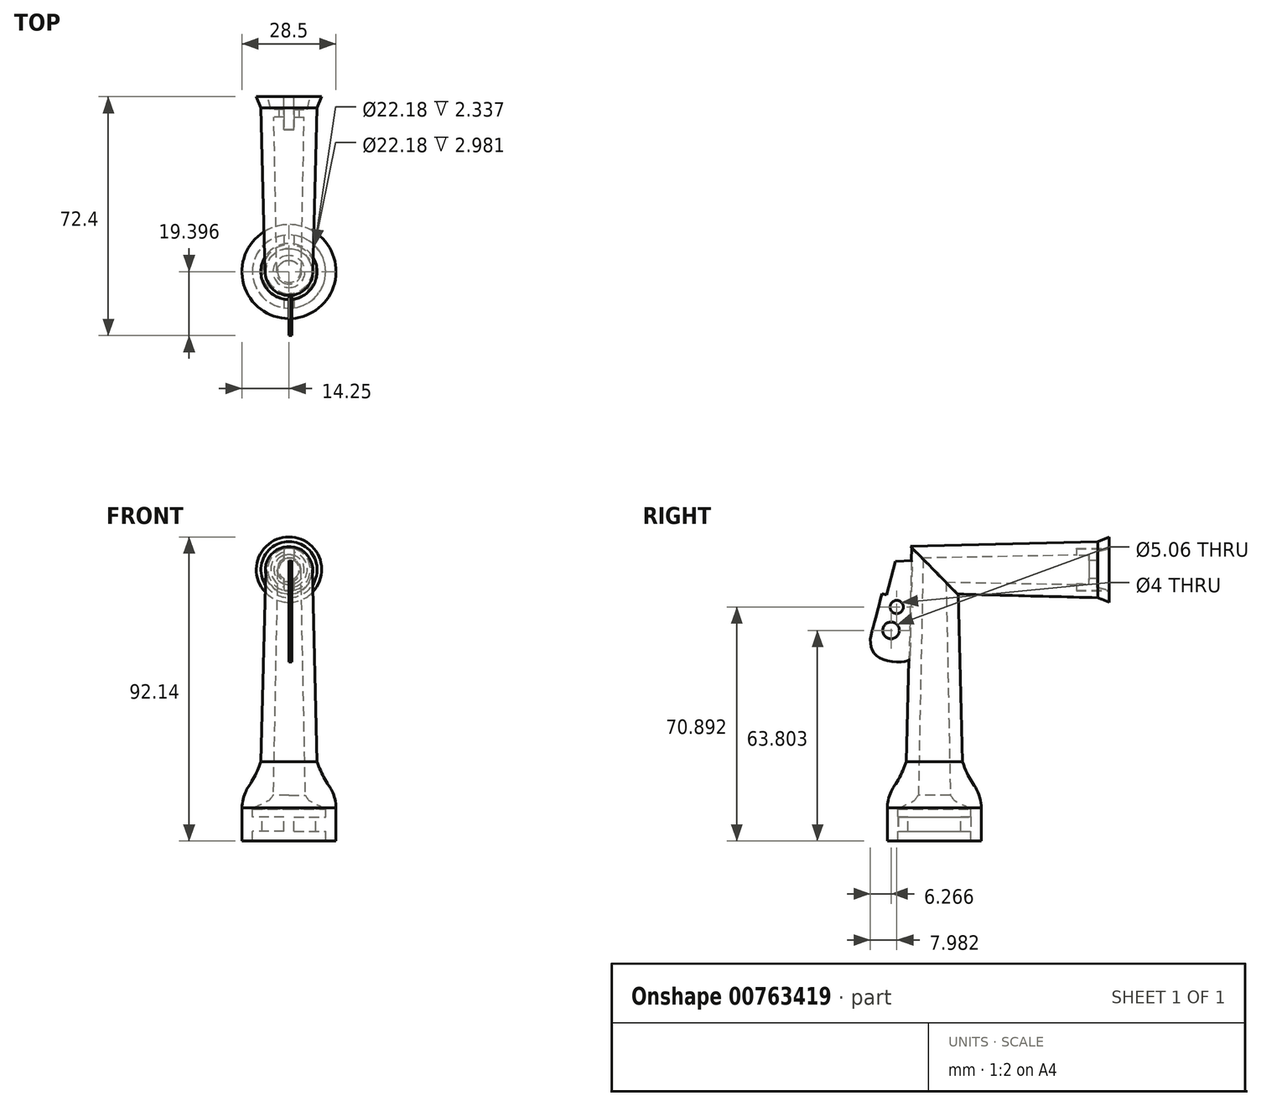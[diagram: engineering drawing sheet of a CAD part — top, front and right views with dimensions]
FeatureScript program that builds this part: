
annotation { "Feature Type Name" : "Feature", "Feature Type Description" : "" }
export const myFeature = defineFeature(function(context is Context, id is Id, definition is map)
    precondition{}
    {
        {
            var Q0;
            Q0=qCreatedBy(makeId("Right.planeOp"),FACE);
            var sketch = newSketch(context, id + "F0", { "sketchPlane" : qUnion([Q0])});
            skLineSegment(sketch, "E0", {"start": v(-40.8, 52.82) * mm, "end": v(-40.8, -26.68) * mm, "construction": true});
            skLineSegment(sketch, "E1", {"start": v(-26.55, -15.77) * mm, "end": v(-26.55, -25.77) * mm});
            skFitSpline(sketch, "E2", {"points": [v(-32.3, -1.7) * mm, v(-30.9, -5.15) * mm, v(-29, -8.6) * mm, v(-27.92, -10.27) * mm, v(-26.85, -13.25) * mm, v(-26.55, -15.77) * mm], "startDerivative": vector(5.6, -15.17) * mm, "endDerivative": vector(0.76, -13.15) * mm});
            skLineSegment(sketch, "E3", {"start": v(-26.55, -25.77) * mm, "end": v(-29.71, -25.77) * mm});
            skLineSegment(sketch, "E4", {"start": v(-29.71, -25.77) * mm, "end": v(-29.71, -22.79) * mm});
            skLineSegment(sketch, "E5", {"start": v(-29.71, -22.79) * mm, "end": v(-32.69, -22.79) * mm});
            skLineSegment(sketch, "E6", {"start": v(-32.69, -22.79) * mm, "end": v(-32.69, -18.47) * mm});
            skLineSegment(sketch, "E7", {"start": v(-32.69, -18.47) * mm, "end": v(-29.71, -18.47) * mm});
            skLineSegment(sketch, "E8", {"start": v(-29.71, -18.47) * mm, "end": v(-29.71, -16.13) * mm});
            skFitSpline(sketch, "E9", {"points": [v(-29.71, -16.13) * mm, v(-31.55, -15.07) * mm, v(-34.67, -13.51) * mm, v(-35.32, -12.81) * mm, v(-35.96, -11.89) * mm], "startDerivative": vector(-6.7, 3.97) * mm, "endDerivative": vector(-3.77, 4.44) * mm});
            skLineSegment(sketch, "E10", {"start": v(-37.46, 63.3) * mm, "end": v(-33.95, 63.38) * mm});
            skLineSegment(sketch, "E11", {"start": v(-33.95, 63.38) * mm, "end": v(-32.3, -1.7) * mm});
            skLineSegment(sketch, "E12", {"start": v(-37.46, 63.3) * mm, "end": v(-35.96, -11.89) * mm});
            skSolve(sketch);
        }
        {
            var Q0;
            Q0=makeQuery(id+"F0.imprint","IMPRINT",FACE,{"disambiguationData":[TD([[makeQuery(id+"F0.imprint","IMPRINT",EDGE,{"derivedFrom":sQuery(id+"F0.wireOp",EDGE,"E1")}),-1.0]])]});
            var Q1;
            Q1=sQuery(id+"F0.wireOp",EDGE,"E0");
            revolve(context, id + "F1", {"surfaceOperationType" : NewSurfaceOperationType.NEW, "entities" : qUnion([Q0]), "axis" : qUnion([Q1]), "revolveType" : RevolveType.FULL});
        }
        {
            var Q0;
            Q0=qCreatedBy(makeId("Right.planeOp"),FACE);
            var sketch = newSketch(context, id + "F2", { "sketchPlane" : qUnion([Q0])});
            skLineSegment(sketch, "E13", {"start": v(-48.14, 31.33) * mm, "end": v(-48.03, 31.27) * mm});
            skLineSegment(sketch, "E14", {"start": v(-48.03, 31.27) * mm, "end": v(-47.41, 59.26) * mm});
            skLineSegment(sketch, "E15", {"start": v(-47.41, 59.26) * mm, "end": v(-54.7, 58.88) * mm});
            skLineSegment(sketch, "E16", {"start": v(-48.14, 29.23) * mm, "end": v(-48.03, 31.27) * mm});
            skFitSpline(sketch, "E17", {"points": [v(-54.7, 56.78) * mm, v(-56.87, 48.48) * mm, v(-59.18, 39.6) * mm, v(-60.2, 34.84) * mm, v(-59.2, 31.3) * mm, v(-56.23, 29.17) * mm, v(-50.78, 28.46) * mm, v(-48.14, 29.23) * mm], "startDerivative": vector(-11.72, -43.94) * mm, "endDerivative": vector(22.2, 9.52) * mm});
            skFitSpline(sketch, "E18", {"points": [v(-54.7, 56.78) * mm, v(-54.7, 58.88) * mm], "startDerivative": vector(0, 2.1) * mm, "endDerivative": vector(0, 2.1) * mm});
            skCircle(sketch, "E19", {"center": v(-53.93, 38.03) * mm, "radius": 2.53 * mm});
            skSolve(sketch);
        }
        {
            var Q0;
            Q0=qSketchRegion(id+"F2",true);
            extrude(context, id + "F3", {"entities" : qUnion([Q0]), "depth" : 0.8 * mm, "offsetDistance" : 25 * mm});
        }
        {
            var Q0;
            Q0=makeQuery(id+"F3.opExtrude","CAP_FACE",FACE,{"disambiguationData":[OSD([sQuery(id+"F2.wireOp",EDGE,"VXiUyJ7P-VCCV-kaxf-uUto-xMQQeP9dgXV0"),sQuery(id+"F2.wireOp",EDGE,"el8HbYCI-KPvh-gZs9-k2xI-aMHFil86eHGo"),sQuery(id+"F2.wireOp",EDGE,"E13"),sQuery(id+"F2.wireOp",EDGE,"E14"),sQuery(id+"F2.wireOp",EDGE,"E15")])],"isStart":false});
            var sketch = newSketch(context, id + "F4", { "sketchPlane" : qUnion([Q0])});
            skCircle(sketch, "E20", {"center": v(-52.22, 45.12) * mm, "radius": 2 * mm});
            skSolve(sketch);
        }
        {
            var Q0;
            Q0=makeQuery(id+"F4.imprint","IMPRINT",FACE,{"disambiguationData":[TD([[makeQuery(id+"F4.imprint","IMPRINT",EDGE,{"derivedFrom":sQuery(id+"F4.wireOp",EDGE,"E20")}),1.0]])]});
            extrude(context, id + "F5", {"entities" : qUnion([Q0]), "operationType" : NewBodyOperationType.REMOVE, "oppositeDirection" : true, "depth" : 25 * mm, "offsetDistance" : 25 * mm});
        }
        {
            var Q0;
            Q0=qCreatedBy(makeId("Front.planeOp"),FACE);
            var sketch = newSketch(context, id + "F6", { "sketchPlane" : qUnion([Q0])});
            skLineSegment(sketch, "E21.bottom", {"start": v(-75.54, 62.8) * mm, "end": v(-43.91, 62.8) * mm});
            skLineSegment(sketch, "E21.top", {"start": v(-75.54, 28.7) * mm, "end": v(-43.91, 28.7) * mm});
            skLineSegment(sketch, "E21.left", {"start": v(-75.54, 62.8) * mm, "end": v(-75.54, 28.7) * mm});
            skLineSegment(sketch, "E21.right", {"start": v(-43.91, 62.8) * mm, "end": v(-43.91, 28.7) * mm});
            skSolve(sketch);
        }
        {
            var Q0;
            Q0=makeQuery(id+"F6.imprint","IMPRINT",FACE,{"disambiguationData":[TD([[makeQuery(id+"F6.imprint","IMPRINT",EDGE,{"derivedFrom":sQuery(id+"F6.wireOp",EDGE,"E21.bottom")}),-1.0]])]});
            extrude(context, id + "F7", {"entities" : qUnion([Q0]), "depth" : 5 * mm, "offsetDistance" : 25 * mm});
        }
        {
            var Q0;
            Q0=makeQuery(id+"F7.opExtrude","SWEPT_BODY",BODY,{"disambiguationData":[OSD([sQuery(id+"F6.wireOp",EDGE,"E21.bottom"),sQuery(id+"F6.wireOp",EDGE,"E21.top"),sQuery(id+"F6.wireOp",EDGE,"E21.left"),sQuery(id+"F6.wireOp",EDGE,"E21.right")])]});
            var Q1;
            Q1=makeQuery(id+"F7.opExtrude","CAP_EDGE",EDGE,{"disambiguationData":[OSD([sQuery(id+"F6.wireOp",EDGE,"E21.bottom")])],"isStart":true});
            transform(context, id + "F8", {"entities" : qUnion([Q0]), "transformType" : TransformType.ROTATION, "transformAxis" : qUnion([Q1]), "angle" : 15 * degree, "oppositeDirection" : true, "makeCopy" : false});
        }
        {
            var Q0;
            Q0=makeQuery(id+"F7.opExtrude","CAP_FACE",FACE,{"disambiguationData":[OSD([sQuery(id+"F6.wireOp",EDGE,"E21.bottom"),sQuery(id+"F6.wireOp",EDGE,"E21.top"),sQuery(id+"F6.wireOp",EDGE,"E21.left"),sQuery(id+"F6.wireOp",EDGE,"E21.right")])],"isStart":false});
            cPlane(context, id + "F9", {"entities" : qUnion([Q0]), "cplaneType" : CPlaneType.OFFSET, "offset" : 51.8 * mm, "width" : 150 * mm, "height" : 150 * mm});
        }
        {
            var Q0;
            Q0=makeQuery(id+"F7.opExtrude","SWEPT_BODY",BODY,{"disambiguationData":[OSD([sQuery(id+"F6.wireOp",EDGE,"E21.bottom"),sQuery(id+"F6.wireOp",EDGE,"E21.top"),sQuery(id+"F6.wireOp",EDGE,"E21.left"),sQuery(id+"F6.wireOp",EDGE,"E21.right")])]});
            transform(context, id + "F10", {"entities" : qUnion([Q0]), "transformType" : TransformType.TRANSLATION_3D, "dx" : -200.4 * mm, "dy" : 0 * mm, "dz" : 0 * mm, "makeCopy" : false});
        }
        {
            var Q0;
            Q0=qCreatedBy(id+"F9.planeOp",FACE);
            var sketch = newSketch(context, id + "F11", { "sketchPlane" : qUnion([Q0])});
            skLineSegment(sketch, "E22.bottom", {"start": v(-1, 45.78) * mm, "end": v(1, 45.78) * mm});
            skLineSegment(sketch, "E22.top", {"start": v(-1, 32.78) * mm, "end": v(1, 32.78) * mm});
            skLineSegment(sketch, "E22.left", {"start": v(-4, 42.78) * mm, "end": v(-4, 35.78) * mm});
            skLineSegment(sketch, "E22.right", {"start": v(4, 42.78) * mm, "end": v(4, 35.78) * mm});
            skPoint(sketch, "E23.visualSharp", {"position": v(-5, 45.38) * mm});
            skArc(sketch, "E23.filletArc", {"start": v(-1, 45.78) * mm, "mid": v(-3.12, 44.9) * mm, "end": v(-4, 42.78) * mm});
            skPoint(sketch, "E24.visualSharp", {"position": v(3, 45.38) * mm});
            skArc(sketch, "E24.filletArc", {"start": v(4, 42.78) * mm, "mid": v(3.12, 44.9) * mm, "end": v(1, 45.78) * mm});
            skPoint(sketch, "E25.visualSharp", {"position": v(3, 32.38) * mm});
            skArc(sketch, "E25.filletArc", {"start": v(1, 32.78) * mm, "mid": v(3.12, 33.66) * mm, "end": v(4, 35.78) * mm});
            skPoint(sketch, "E26.visualSharp", {"position": v(-5, 32.38) * mm});
            skArc(sketch, "E26.filletArc", {"start": v(-4, 35.78) * mm, "mid": v(-3.12, 33.66) * mm, "end": v(-1, 32.78) * mm});
            skSolve(sketch);
        }
        {
            var Q0;
            Q0=makeQuery(id+"F11.imprint","IMPRINT",FACE,{"disambiguationData":[TD([[makeQuery(id+"F11.imprint","IMPRINT",EDGE,{"derivedFrom":sQuery(id+"F11.wireOp",EDGE,"E22.bottom")}),-1.0]])]});
            extrude(context, id + "F12", {"entities" : qUnion([Q0]), "operationType" : NewBodyOperationType.REMOVE, "oppositeDirection" : true, "depth" : 7 * mm, "offsetDistance" : 25 * mm});
        }
        {
            var Q0;
            Q0=makeQuery(id+"F7.opExtrude","SWEPT_BODY",BODY,{"disambiguationData":[OSD([sQuery(id+"F6.wireOp",EDGE,"E21.bottom"),sQuery(id+"F6.wireOp",EDGE,"E21.top"),sQuery(id+"F6.wireOp",EDGE,"E21.left"),sQuery(id+"F6.wireOp",EDGE,"E21.right")])]});
            var Q1;
            Q1=makeQuery(id+"Flpr5LHeYpND3I0_4.opExtrude","SWEPT_BODY",BODY,{"disambiguationData":[OSD([sQuery(id+"FyDyzudHODPkHYP_4.wireOp",EDGE,"m75Vnbgv-jhCc-RTIO-U7NT-55jqRwHsRLKe.bottom"),sQuery(id+"FyDyzudHODPkHYP_4.wireOp",EDGE,"m75Vnbgv-jhCc-RTIO-U7NT-55jqRwHsRLKe.top"),sQuery(id+"FyDyzudHODPkHYP_4.wireOp",EDGE,"m75Vnbgv-jhCc-RTIO-U7NT-55jqRwHsRLKe.left"),sQuery(id+"FyDyzudHODPkHYP_4.wireOp",EDGE,"m75Vnbgv-jhCc-RTIO-U7NT-55jqRwHsRLKe.right")])]});
            deleteBodies(context, id + "F13", {"entities" : qUnion([Q0, Q1])});
        }
        {
            var Q0;
            Q0=qCreatedBy(makeId("Right.planeOp"),FACE);
            cPlane(context, id + "F14", {"entities" : qUnion([Q0]), "cplaneType" : CPlaneType.OFFSET, "offset" : 10.2 * mm, "width" : 150 * mm, "height" : 150 * mm});
        }
        {
            var Q0;
            Q0=qCreatedBy(makeId("Right.planeOp"),FACE);
            var sketch = newSketch(context, id + "F15", { "sketchPlane" : qUnion([Q0])});
            skLineSegment(sketch, "E27", {"start": v(-45.77, 56.46) * mm, "end": v(33.73, 56.46) * mm, "construction": true});
            skLineSegment(sketch, "E28", {"start": v(-48.05, 60.02) * mm, "end": v(-48.14, 63.53) * mm});
            skLineSegment(sketch, "E29", {"start": v(-48.14, 63.53) * mm, "end": v(8.76, 64.97) * mm});
            skLineSegment(sketch, "E30", {"start": v(12.2, 66.37) * mm, "end": v(12.2, 62.93) * mm});
            skLineSegment(sketch, "E31", {"start": v(12.2, 62.93) * mm, "end": v(8.34, 61.99) * mm});
            skLineSegment(sketch, "E32", {"start": v(8.34, 61.99) * mm, "end": v(8.34, 59.55) * mm});
            skLineSegment(sketch, "E33", {"start": v(8.34, 59.55) * mm, "end": v(6, 59.55) * mm});
            skLineSegment(sketch, "E34", {"start": v(6, 59.55) * mm, "end": v(6, 61.06) * mm});
            skLineSegment(sketch, "E35", {"start": v(6, 61.06) * mm, "end": v(-48.05, 60.02) * mm});
            skLineSegment(sketch, "E36", {"start": v(8.76, 64.97) * mm, "end": v(12.2, 66.37) * mm});
            skSolve(sketch);
        }
        {
            var Q0;
            Q0=makeQuery(id+"F15.imprint","IMPRINT",FACE,{"disambiguationData":[TD([[makeQuery(id+"F15.imprint","IMPRINT",EDGE,{"derivedFrom":sQuery(id+"F15.wireOp",EDGE,"E28")}),-1.0]])]});
            var Q1;
            Q1=sQuery(id+"F15.wireOp",EDGE,"E27");
            revolve(context, id + "F16", {"surfaceOperationType" : NewSurfaceOperationType.NEW, "entities" : qUnion([Q0]), "axis" : qUnion([Q1]), "revolveType" : RevolveType.FULL});
        }
        {
            var Q0;
            Q0=qCreatedBy(id+"F14.planeOp",FACE);
            var sketch = newSketch(context, id + "F17", { "sketchPlane" : qUnion([Q0])});
            skLineSegment(sketch, "E37", {"start": v(-48.76, 64.23) * mm, "end": v(-32.73, 47.94) * mm});
            skLineSegment(sketch, "E38", {"start": v(-32.73, 47.94) * mm, "end": v(-49.67, 47.94) * mm});
            skLineSegment(sketch, "E39", {"start": v(-49.67, 47.94) * mm, "end": v(-48.76, 64.23) * mm});
            skSolve(sketch);
        }
        {
            var Q0;
            Q0=makeQuery(id+"F17.imprint","IMPRINT",FACE,{"disambiguationData":[TD([[makeQuery(id+"F17.imprint","IMPRINT",EDGE,{"derivedFrom":sQuery(id+"F17.wireOp",EDGE,"E37")}),-1.0]])]});
            extrude(context, id + "F18", {"entities" : qUnion([Q0]), "oppositeDirection" : true, "depth" : 25 * mm, "offsetDistance" : 25 * mm});
        }
        {
            var Q0;
            Q0=makeQuery(id+"F18.opExtrude","SWEPT_BODY",BODY,{"disambiguationData":[OSD([sQuery(id+"F17.wireOp",EDGE,"E37"),sQuery(id+"F17.wireOp",EDGE,"E38"),sQuery(id+"F17.wireOp",EDGE,"E39")])]});
            var Q1;
            Q1=makeQuery(id+"F16.opRevolve","SWEPT_BODY",BODY,{"disambiguationData":[OSD([sQuery(id+"F15.wireOp",EDGE,"E28"),sQuery(id+"F15.wireOp",EDGE,"E29"),sQuery(id+"F15.wireOp",EDGE,"E30"),sQuery(id+"F15.wireOp",EDGE,"E31"),sQuery(id+"F15.wireOp",EDGE,"E32"),sQuery(id+"F15.wireOp",EDGE,"E33"),sQuery(id+"F15.wireOp",EDGE,"E34"),sQuery(id+"F15.wireOp",EDGE,"E35"),sQuery(id+"F15.wireOp",EDGE,"E36")])]});
            booleanBodies(context, id + "F19", {"operationType" : BooleanOperationType.SUBTRACTION, "tools" : qUnion([Q0]), "targets" : qUnion([Q1])});
        }
        {
            var Q0;
            Q0=qCreatedBy(id+"F14.planeOp",FACE);
            var sketch = newSketch(context, id + "F20", { "sketchPlane" : qUnion([Q0])});
            skLineSegment(sketch, "E40", {"start": v(-48, 63.74) * mm, "end": v(-32.69, 48.2) * mm});
            skLineSegment(sketch, "E41", {"start": v(-32.69, 48.2) * mm, "end": v(-32.69, 64.7) * mm});
            skLineSegment(sketch, "E42", {"start": v(-32.69, 64.7) * mm, "end": v(-48, 63.74) * mm});
            skSolve(sketch);
        }
        {
            var Q0;
            Q0=makeQuery(id+"F20.imprint","IMPRINT",FACE,{"disambiguationData":[TD([[makeQuery(id+"F20.imprint","IMPRINT",EDGE,{"derivedFrom":sQuery(id+"F20.wireOp",EDGE,"E40")}),1.0]])]});
            extrude(context, id + "F21", {"entities" : qUnion([Q0]), "oppositeDirection" : true, "depth" : 25 * mm, "offsetDistance" : 25 * mm});
        }
        {
            var Q0;
            Q0=makeQuery(id+"F21.opExtrude","SWEPT_BODY",BODY,{"disambiguationData":[OSD([sQuery(id+"F20.wireOp",EDGE,"E40"),sQuery(id+"F20.wireOp",EDGE,"E41"),sQuery(id+"F20.wireOp",EDGE,"E42")])]});
            var Q1;
            Q1=makeQuery(id+"F1.opRevolve","SWEPT_BODY",BODY,{"disambiguationData":[OSD([sQuery(id+"F0.wireOp",EDGE,"E1"),sQuery(id+"F0.wireOp",EDGE,"E2"),sQuery(id+"F0.wireOp",EDGE,"E3"),sQuery(id+"F0.wireOp",EDGE,"E4"),sQuery(id+"F0.wireOp",EDGE,"E5"),sQuery(id+"F0.wireOp",EDGE,"E6"),sQuery(id+"F0.wireOp",EDGE,"E7"),sQuery(id+"F0.wireOp",EDGE,"E8"),sQuery(id+"F0.wireOp",EDGE,"E9"),sQuery(id+"F0.wireOp",EDGE,"E10"),sQuery(id+"F0.wireOp",EDGE,"E11"),sQuery(id+"F0.wireOp",EDGE,"E12")])]});
            booleanBodies(context, id + "F22", {"operationType" : BooleanOperationType.SUBTRACTION, "tools" : qUnion([Q0]), "targets" : qUnion([Q1])});
        }
        {
            var Q0;
            Q0=makeQuery(id+"F1.opRevolve","SWEPT_FACE",FACE,{"disambiguationData":[OSD([sQuery(id+"F0.wireOp",EDGE,"E5")])]});
            var sketch = newSketch(context, id + "F23", { "sketchPlane" : qUnion([Q0])});
            skLineSegment(sketch, "E43", {"start": v(-1.5, 51.8) * mm, "end": v(-1.5, 29.81) * mm});
            skLineSegment(sketch, "E44", {"start": v(1.5, 51.8) * mm, "end": v(1.5, 29.81) * mm});
            skArc(sketch, "E45", {"start": v(-1.5, 29.81) * mm, "mid": v(0, 29.7) * mm, "end": v(1.5, 29.81) * mm});
            skArc(sketch, "E46", {"start": v(1.5, 51.8) * mm, "mid": v(0, 51.9) * mm, "end": v(-1.5, 51.8) * mm});
            skSolve(sketch);
        }
        {
            var Q0;
            Q0 = qSketchRegion(id + "F23", true);
            extrude(context, id + "F24", {"entities" : qUnion([Q0]), "operationType" : NewBodyOperationType.REMOVE, "oppositeDirection" : true, "depth" : 4.4 * mm, "offsetDistance" : 25 * mm});
        }
        {
            var Q0;
            Q0=makeQuery(id+"F16.opRevolve","SWEPT_FACE",FACE,{"disambiguationData":[OSD([sQuery(id+"F15.wireOp",EDGE,"E30")])]});
            var sketch = newSketch(context, id + "F25", { "sketchPlane" : qUnion([Q0])});
            skLineSegment(sketch, "E47", {"start": v(-1.5, 62.75) * mm, "end": v(-1.5, 50.18) * mm});
            skLineSegment(sketch, "E48", {"start": v(1.5, 62.75) * mm, "end": v(1.5, 50.18) * mm});
            skArc(sketch, "E49", {"start": v(1.5, 62.75) * mm, "mid": v(0, 62.94) * mm, "end": v(-1.5, 62.75) * mm});
            skArc(sketch, "E50", {"start": v(-1.5, 50.18) * mm, "mid": v(0, 50) * mm, "end": v(1.5, 50.18) * mm});
            skSolve(sketch);
        }
        {
            var Q0;
            {var subQ0=sQuery(id+"F25.wireOp",EDGE,"E47");Q0=makeQuery(id+"F25.imprint","IMPRINT",FACE,{"disambiguationData":[TD([[makeQuery(id+"F25.imprint","IMPRINT",EDGE,{"derivedFrom":subQ0}),1.0]])]});}
            extrude(context, id + "F26", {"entities" : qUnion([Q0]), "operationType" : NewBodyOperationType.REMOVE, "oppositeDirection" : true, "depth" : 10 * mm, "offsetDistance" : 25 * mm});
        }
    });
